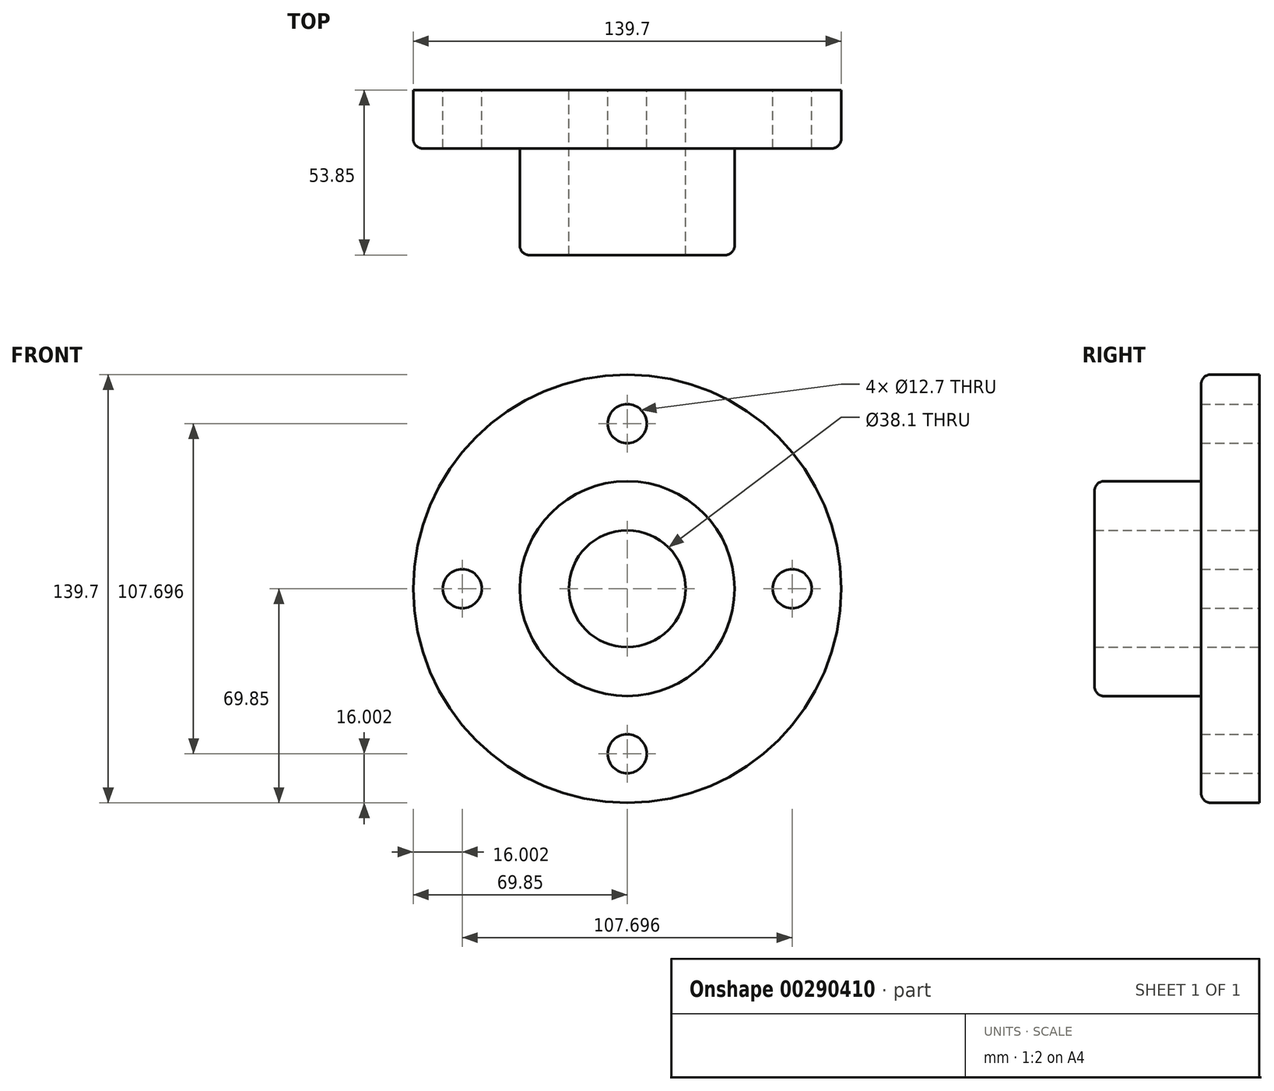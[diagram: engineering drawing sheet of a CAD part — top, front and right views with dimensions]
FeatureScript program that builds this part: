
annotation { "Feature Type Name" : "Feature", "Feature Type Description" : "" }
export const myFeature = defineFeature(function(context is Context, id is Id, definition is map)
    precondition{}
    {
        {
            var Q0;
            Q0=qCreatedBy(makeId("Front.planeOp"),FACE);
            var sketch = newSketch(context, id + "F0", { "sketchPlane" : qUnion([Q0])});
            skCircle(sketch, "E0", {"center": v(0, 0) * mm, "radius": 19.05 * mm});
            skCircle(sketch, "E1", {"center": v(0, 0) * mm, "radius": 35.05 * mm});
            skCircle(sketch, "E2", {"center": v(0, 0) * mm, "radius": 53.85 * mm});
            skCircle(sketch, "E3", {"center": v(0, 0) * mm, "radius": 69.85 * mm});
            skCircle(sketch, "E4", {"center": v(0, 53.85) * mm, "radius": 6.35 * mm});
            skCircle(sketch, "E5", {"center": v(53.85, 0) * mm, "radius": 6.35 * mm});
            skCircle(sketch, "E6", {"center": v(0, -53.85) * mm, "radius": 6.35 * mm});
            skCircle(sketch, "E7", {"center": v(-53.85, 0) * mm, "radius": 6.35 * mm});
            skSolve(sketch);
        }
        {
            var Q0;
            Q0=makeQuery(id+"F0.imprint","IMPRINT",FACE,{"disambiguationData":[TD([[makeQuery(id+"F0.imprint","IMPRINT",EDGE,{"derivedFrom":sQuery(id+"F0.wireOp",EDGE,"E0")}),-1.0]])]});
            extrude(context, id + "F1", {"entities" : qUnion([Q0]), "depth" : 53.85 * mm});
        }
        {
            var Q0;
            Q0=makeQuery(id+"F0.imprint","IMPRINT",FACE,{"disambiguationData":[TD([[makeQuery(id+"F0.imprint","IMPRINT",EDGE,{"derivedFrom":sQuery(id+"F0.wireOp",EDGE,"E1")}),-1.0]])]});
            var Q1;
            Q1=makeQuery(id+"F0.imprint","IMPRINT",FACE,{"disambiguationData":[TD([[makeQuery(id+"F0.imprint","IMPRINT",EDGE,{"derivedFrom":sQuery(id+"F0.wireOp",EDGE,"E3")}),1.0]])]});
            extrude(context, id + "F2", {"entities" : qUnion([Q0, Q1]), "operationType" : NewBodyOperationType.ADD, "depth" : 19.05 * mm});
        }
        {
            var Q0;
            Q0=makeQuery(id+"F1.opExtrude","CAP_EDGE",EDGE,{"disambiguationData":[OSD([sQuery(id+"F0.wireOp",EDGE,"E1")])],"isStart":false});
            var Q1;
            Q1=makeQuery(id+"F2.opExtrude","CAP_EDGE",EDGE,{"disambiguationData":[OSD([sQuery(id+"F0.wireOp",EDGE,"E1")])],"isStart":false});
            var Q2;
            Q2=makeQuery(id+"F2.opExtrude","CAP_EDGE",EDGE,{"disambiguationData":[OSD([sQuery(id+"F0.wireOp",EDGE,"E3")])],"isStart":false});
            fillet(context, id + "F3", {"entities" : qUnion([Q0, Q1, Q2]), "radius" : 3.05 * mm, "tangentPropagation" : true, "allowEdgeOverflow" : false});
        }
    });
